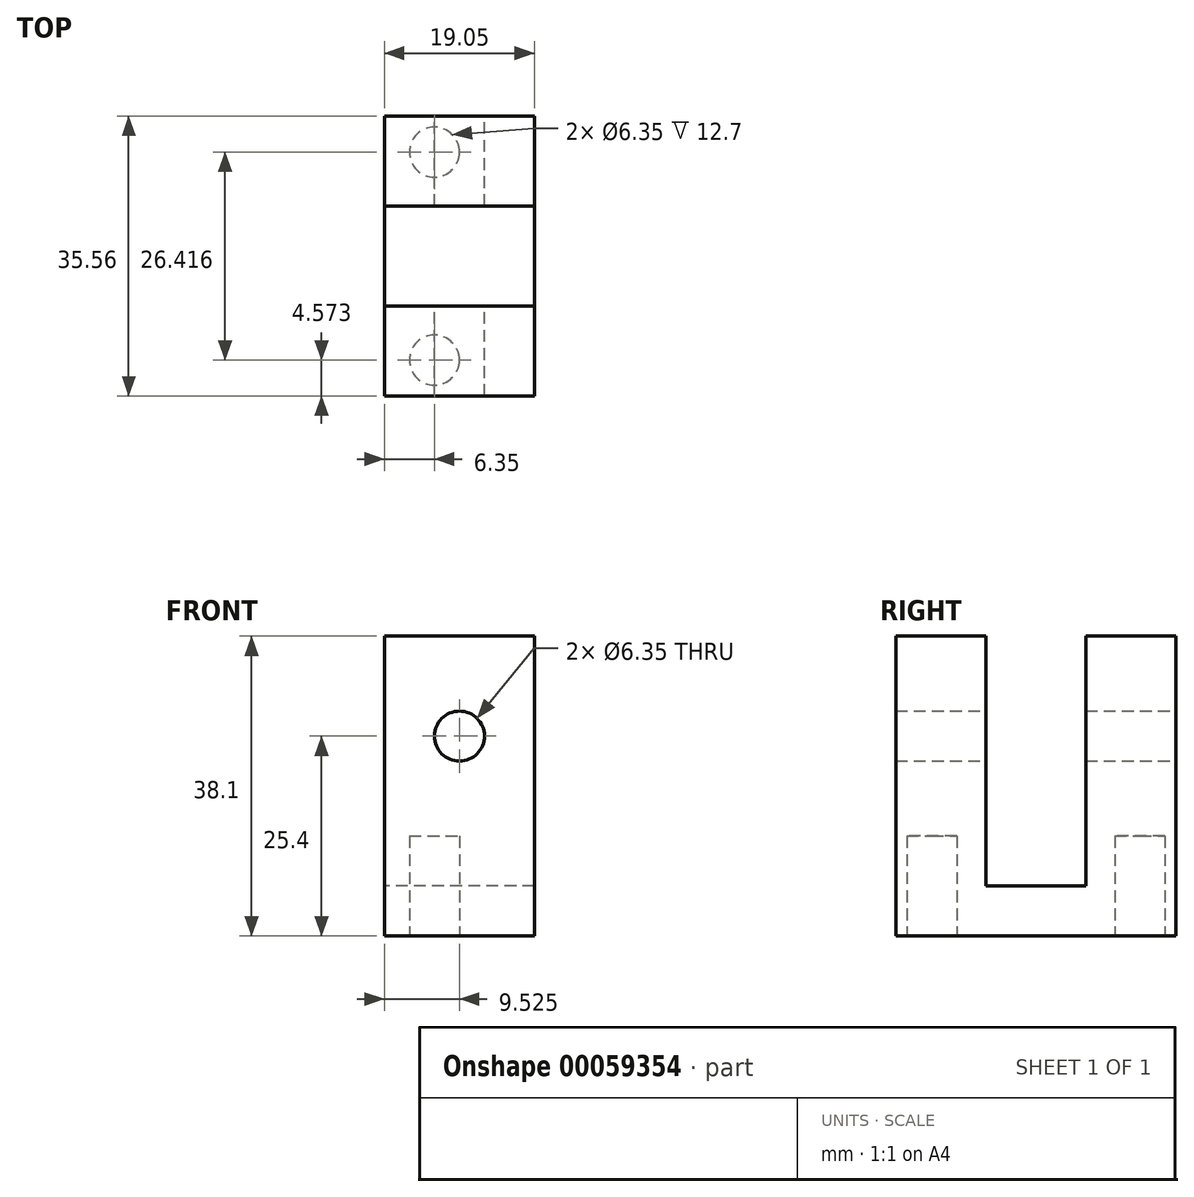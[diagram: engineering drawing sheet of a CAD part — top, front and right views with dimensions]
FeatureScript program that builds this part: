
annotation { "Feature Type Name" : "Feature", "Feature Type Description" : "" }
export const myFeature = defineFeature(function(context is Context, id is Id, definition is map)
    precondition{}
    {
        {
            var Q0;
            Q0=qCreatedBy(makeId("Right.planeOp"),FACE);
            var sketch = newSketch(context, id + "F0", { "sketchPlane" : qUnion([Q0])});
            skLineSegment(sketch, "E0.top", {"start": v(-17.8, 0) * mm, "end": v(17.75, 0) * mm});
            skLineSegment(sketch, "E0.left", {"start": v(-17.8, 38.1) * mm, "end": v(-17.8, 0) * mm});
            skLineSegment(sketch, "E0.right", {"start": v(17.75, 38.1) * mm, "end": v(17.75, 0) * mm});
            skLineSegment(sketch, "E1.top", {"start": v(-6.38, 6.35) * mm, "end": v(6.32, 6.35) * mm});
            skLineSegment(sketch, "E1.left", {"start": v(-6.38, 38.1) * mm, "end": v(-6.38, 6.35) * mm});
            skLineSegment(sketch, "E1.right", {"start": v(6.32, 38.1) * mm, "end": v(6.32, 6.35) * mm});
            skLineSegment(sketch, "E2.trimOffspring", {"start": v(6.32, 38.1) * mm, "end": v(17.75, 38.1) * mm});
            skLineSegment(sketch, "E3", {"start": v(-17.8, 38.1) * mm, "end": v(-6.38, 38.1) * mm});
            skSolve(sketch);
        }
        {
            var Q0;
            Q0=makeQuery(id+"F0.imprint","IMPRINT",FACE,{"disambiguationData":[TD([[makeQuery(id+"F0.imprint","IMPRINT",EDGE,{"derivedFrom":sQuery(id+"F0.wireOp",EDGE,"E0.top")}),1.0]])]});
            extrude(context, id + "F1", {"entities" : qUnion([Q0]), "depth" : 19.05 * mm});
        }
        {
            var Q0;
            Q0=makeQuery(id+"F1.opExtrude","SWEPT_FACE",FACE,{"disambiguationData":[OSD([sQuery(id+"F0.wireOp",EDGE,"E0.right")])]});
            var sketch = newSketch(context, id + "F2", { "sketchPlane" : qUnion([Q0])});
            skCircle(sketch, "E4", {"center": v(-9.53, 25.4) * mm, "radius": 3.18 * mm});
            skPoint(sketch, "E4.centerSnap0", {"position": v(-9.53, 38.1) * mm});
            skSolve(sketch);
        }
        {
            var Q0;
            Q0=sQuery(id+"F2.wireOp",VERTEX,"E4.center");
            var Q1;
            Q1=makeQuery(id+"F1.opExtrude","SWEPT_BODY",BODY,{"disambiguationData":[OSD([sQuery(id+"F0.wireOp",EDGE,"E0.top"),sQuery(id+"F0.wireOp",EDGE,"E0.left"),sQuery(id+"F0.wireOp",EDGE,"E0.right"),sQuery(id+"F0.wireOp",EDGE,"E1.top"),sQuery(id+"F0.wireOp",EDGE,"E1.left"),sQuery(id+"F0.wireOp",EDGE,"E1.right"),sQuery(id+"F0.wireOp",EDGE,"E2.trimOffspring"),sQuery(id+"F0.wireOp",EDGE,"E3")])]});
            hole(context, id + "F3", {"style" : HoleStyle.SIMPLE, "holeDiameter" : 6.35 * mm, "endStyle" : HoleEndStyle.THROUGH, "locations" : qUnion([Q0]), "scope" : qUnion([Q1])});
        }
        {
            var Q0;
            Q0=makeQuery(id+"F1.opExtrude","SWEPT_FACE",FACE,{"disambiguationData":[OSD([sQuery(id+"F0.wireOp",EDGE,"E0.top")])]});
            var sketch = newSketch(context, id + "F4", { "sketchPlane" : qUnion([Q0])});
            skCircle(sketch, "E5", {"center": v(6.35, 13.24) * mm, "radius": 3.18 * mm});
            skCircle(sketch, "E6", {"center": v(6.35, -13.18) * mm, "radius": 3.18 * mm});
            skSolve(sketch);
        }
        {
            var Q0;
            Q0 = qSketchRegion(id + "F4", true);
            extrude(context, id + "F5", {"entities" : qUnion([Q0]), "operationType" : NewBodyOperationType.REMOVE, "oppositeDirection" : true, "depth" : 12.7 * mm});
        }
    });
